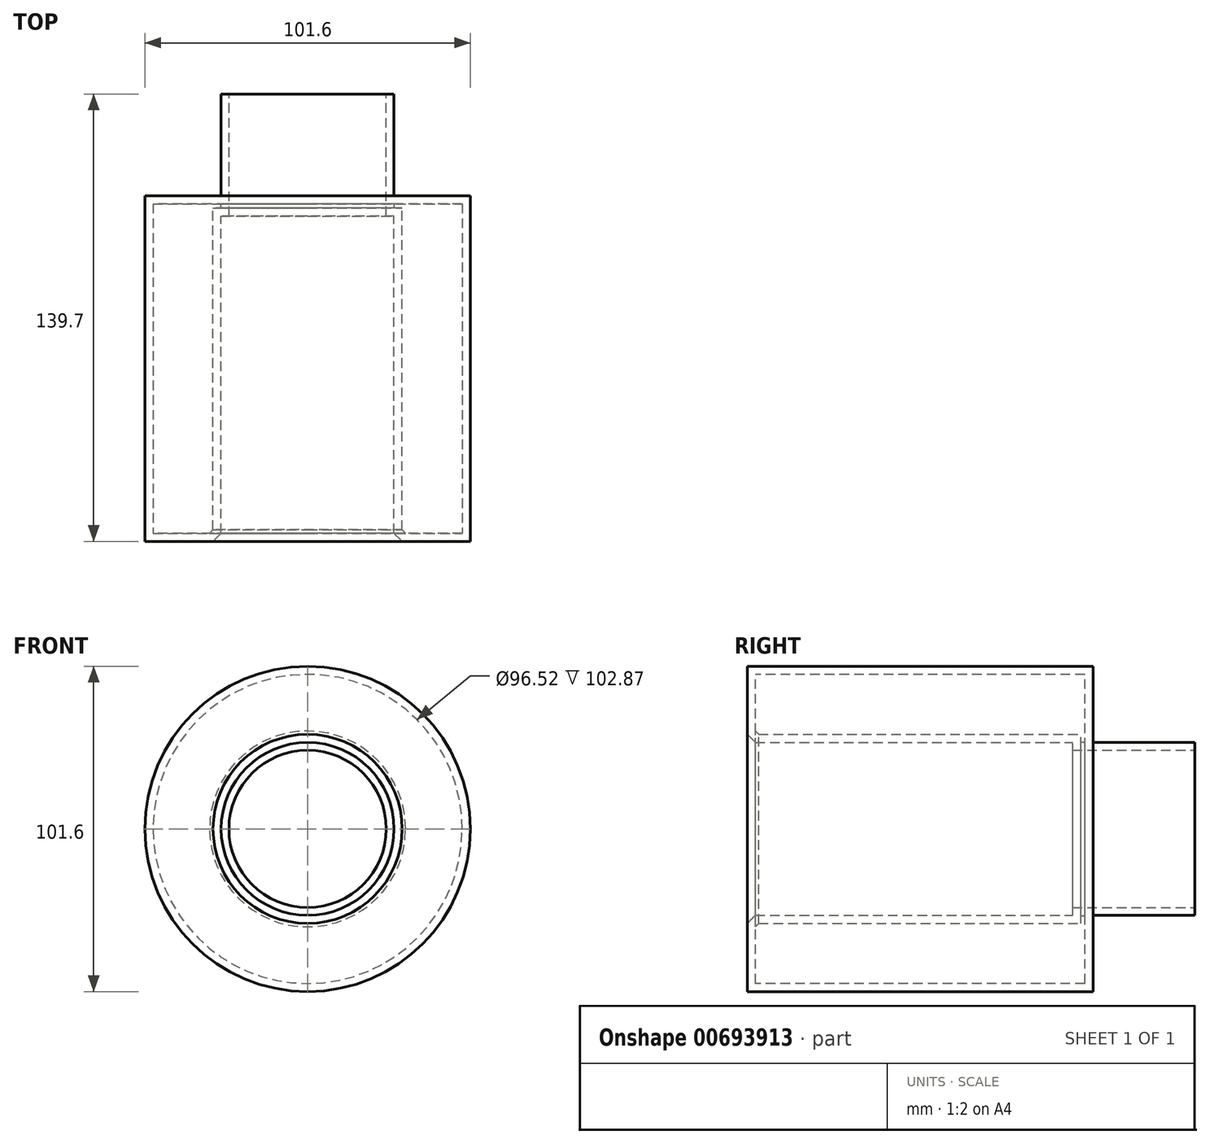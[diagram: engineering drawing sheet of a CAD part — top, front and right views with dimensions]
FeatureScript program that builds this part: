
annotation { "Feature Type Name" : "Feature", "Feature Type Description" : "" }
export const myFeature = defineFeature(function(context is Context, id is Id, definition is map)
    precondition{}
    {
        {
            var Q0;
            Q0=qCreatedBy(makeId("Front.planeOp"),FACE);
            var sketch = newSketch(context, id + "F0", { "sketchPlane" : qUnion([Q0])});
            skCircle(sketch, "E0", {"center": v(0, 0) * mm, "radius": 50.8 * mm});
            skCircle(sketch, "E1", {"center": v(0, 0) * mm, "radius": 26.99 * mm});
            skSolve(sketch);
        }
        {
            var Q0;
            Q0=makeQuery(id+"F0.imprint","IMPRINT",FACE,{"disambiguationData":[TD([[makeQuery(id+"F0.imprint","IMPRINT",EDGE,{"derivedFrom":sQuery(id+"F0.wireOp",EDGE,"1775f497-705d-43bd-ad04-4306bf6ceec5")}),1.0]])]});
            var Q1;
            Q1=makeQuery(id+"F0.imprint","IMPRINT",FACE,{"disambiguationData":[TD([[makeQuery(id+"F0.imprint","IMPRINT",EDGE,{"derivedFrom":sQuery(id+"F0.wireOp",EDGE,"E1")}),1.0]])]});
            extrude(context, id + "F1", {"entities" : qUnion([Q0, Q1]), "oppositeDirection" : true, "depth" : 38.1 * mm, "offsetDistance" : 25.4 * mm});
        }
        {
            var Q0;
            Q0=makeQuery(id+"F0.imprint","IMPRINT",FACE,{"disambiguationData":[TD([[makeQuery(id+"F0.imprint","IMPRINT",EDGE,{"derivedFrom":sQuery(id+"F0.wireOp",EDGE,"E0")}),1.0]])]});
            extrude(context, id + "F2", {"entities" : qUnion([Q0]), "operationType" : NewBodyOperationType.ADD, "oppositeDirection" : true, "depth" : 6.35 * mm, "offsetDistance" : 25.4 * mm});
        }
        {
            var Q0;
            Q0=makeQuery(id+"F0.imprint","IMPRINT",FACE,{"disambiguationData":[TD([[makeQuery(id+"F0.imprint","IMPRINT",EDGE,{"derivedFrom":sQuery(id+"F0.wireOp",EDGE,"E0")}),1.0]])]});
            extrude(context, id + "F3", {"entities" : qUnion([Q0]), "operationType" : NewBodyOperationType.ADD, "depth" : 101.6 * mm, "offsetDistance" : 25.4 * mm});
        }
        {
            var Q0;
            Q0=makeQuery(id+"F1.opExtrude","CAP_FACE",FACE,{"disambiguationData":[OSD([sQuery(id+"F0.wireOp",EDGE,"E1")])],"isStart":false});
            var sketch = newSketch(context, id + "F4", { "sketchPlane" : qUnion([Q0])});
            skCircle(sketch, "E2", {"center": v(0, 0) * mm, "radius": 24.56 * mm});
            skSolve(sketch);
        }
        {
            var Q0;
            Q0=makeQuery(id+"F4.imprint","IMPRINT",FACE,{"disambiguationData":[TD([[makeQuery(id+"F4.imprint","IMPRINT",EDGE,{"derivedFrom":sQuery(id+"F4.wireOp",EDGE,"E2")}),1.0]])]});
            extrude(context, id + "F5", {"entities" : qUnion([Q0]), "operationType" : NewBodyOperationType.REMOVE, "oppositeDirection" : true, "depth" : 127 * mm, "offsetDistance" : 25.4 * mm});
        }
        {
            var Q0;
            Q0=makeQuery(id+"F3.opExtrude","CAP_EDGE",EDGE,{"disambiguationData":[OSD([sQuery(id+"F0.wireOp",EDGE,"E1")])],"isStart":false});
            chamfer(context, id + "F6", {"entities" : qUnion([Q0]), "chamferType" : ChamferType.TWO_OFFSETS, "width1" : 2.54 * mm, "oppositeDirection" : false, "width2" : 2.54 * mm, "tangentPropagation" : true});
        }
        {
            var Q0;
            Q0=makeQuery(id+"F1.opExtrude","SWEPT_FACE",FACE,{"disambiguationData":[OSD([sQuery(id+"F0.wireOp",EDGE,"E1")])]});
            var Q1;
            Q1=makeQuery(id+"F1.opExtrude","SWEPT_BODY",BODY,{"disambiguationData":[OSD([sQuery(id+"F0.wireOp",EDGE,"E1")])]});
            shell(context, id + "F7", {"isHollow" : true, "entities" : qUnion([Q0]), "parts" : qUnion([Q1]), "thickness" : 2.54 * mm});
        }
    });
